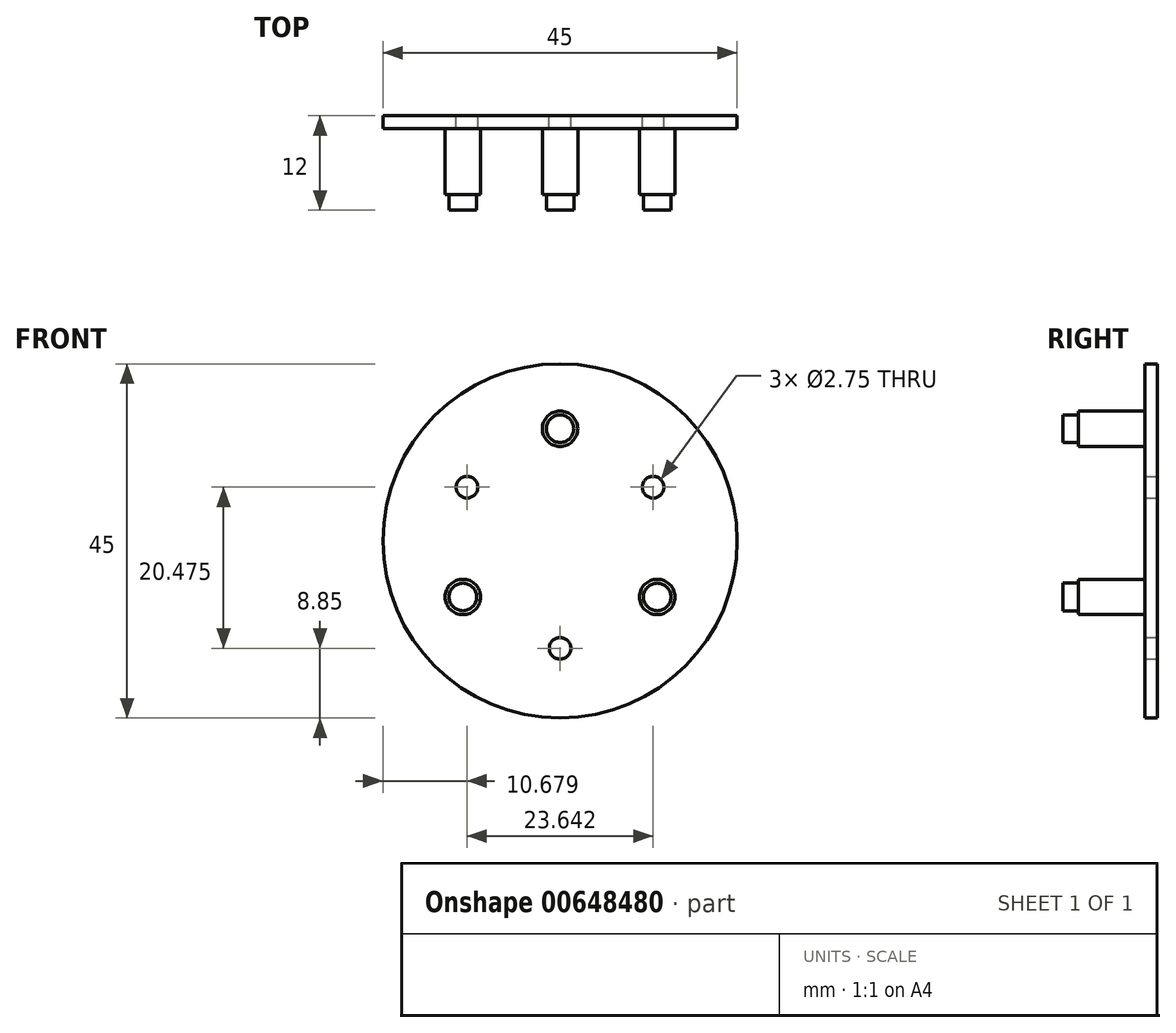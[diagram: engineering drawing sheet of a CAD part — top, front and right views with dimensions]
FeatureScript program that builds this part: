
annotation { "Feature Type Name" : "Feature", "Feature Type Description" : "" }
export const myFeature = defineFeature(function(context is Context, id is Id, definition is map)
    precondition{}
    {
        {
            var Q0;
            Q0=qCreatedBy(makeId("Front.planeOp"),FACE);
            var sketch = newSketch(context, id + "F0", { "sketchPlane" : qUnion([Q0])});
            skCircle(sketch, "E0", {"center": v(0, 0) * mm, "radius": 22.5 * mm});
            skSolve(sketch);
        }
        {
            var Q0;
            Q0=makeQuery(id+"F0.imprint","IMPRINT",FACE,{"disambiguationData":[TD([[makeQuery(id+"F0.imprint","IMPRINT",EDGE,{"derivedFrom":sQuery(id+"F0.wireOp",EDGE,"E0")}),1.0]])]});
            extrude(context, id + "F1", {"entities" : qUnion([Q0]), "depth" : 1.6 * mm, "offsetDistance" : 25 * mm});
        }
        {
            var Q0;
            Q0=makeQuery(id+"F1.opExtrude","CAP_FACE",FACE,{"disambiguationData":[OSD([sQuery(id+"F0.wireOp",EDGE,"E0")])],"isStart":true});
            var sketch = newSketch(context, id + "F2", { "sketchPlane" : qUnion([Q0])});
            skPoint(sketch, "E1", {"position": v(0, 14.25) * mm});
            skPoint(sketch, "E2.1.0", {"position": v(-12.34, -7.12) * mm});
            skPoint(sketch, "E2.2.0", {"position": v(12.34, -7.13) * mm});
            skPoint(sketch, "E2.center", {"position": v(0, 0) * mm});
            skCircle(sketch, "E3", {"center": v(0, 14.25) * mm, "radius": 2.25 * mm});
            skCircle(sketch, "E4", {"center": v(-12.34, -7.12) * mm, "radius": 2.25 * mm});
            skCircle(sketch, "E5", {"center": v(12.34, -7.13) * mm, "radius": 2.25 * mm});
            skSolve(sketch);
        }
        {
            var Q0;
            Q0=makeQuery(id+"F1.opExtrude","CAP_FACE",FACE,{"disambiguationData":[OSD([sQuery(id+"F0.wireOp",EDGE,"E0")])],"isStart":true});
            var sketch = newSketch(context, id + "F3", { "sketchPlane" : qUnion([Q0])});
            skPoint(sketch, "E6", {"position": v(0, -13.65) * mm});
            skPoint(sketch, "E7.1.0", {"position": v(11.82, 6.82) * mm});
            skPoint(sketch, "E7.2.0", {"position": v(-11.82, 6.83) * mm});
            skPoint(sketch, "E7.center", {"position": v(0, 0) * mm});
            skSolve(sketch);
        }
        {
            var Q0;
            Q0=sQuery(id+"F3.wireOp",VERTEX,"E7.1.0");
            var Q1;
            Q1=sQuery(id+"F3.wireOp",VERTEX,"E6");
            var Q2;
            Q2=sQuery(id+"F3.wireOp",VERTEX,"E7.2.0");
            var Q3;
            Q3=makeQuery(id+"F1.opExtrude","SWEPT_BODY",BODY,{"disambiguationData":[OSD([sQuery(id+"F0.wireOp",EDGE,"E0")])]});
            hole(context, id + "F4", {"style" : HoleStyle.SIMPLE, "endStyle" : HoleEndStyle.THROUGH, "holeDiameter" : 2.75 * mm, "majorDiameter" : 5 * mm, "isTappedThrough" : true, "tappedDepth" : 12 * mm, "tapClearance" : 3, "locations" : qUnion([Q0, Q1, Q2]), "scope" : qUnion([Q3])});
        }
        {
            var Q0;
            Q0 = qSketchRegion(id + "F2", true);
            extrude(context, id + "F5", {"entities" : qUnion([Q0]), "operationType" : NewBodyOperationType.ADD, "oppositeDirection" : true, "depth" : 10 * mm, "offsetDistance" : 25 * mm});
        }
        {
            var Q0;
            Q0=makeQuery(id+"F5.opExtrude","CAP_FACE",FACE,{"disambiguationData":[OSD([sQuery(id+"F2.wireOp",EDGE,"E3")])],"isStart":false});
            var sketch = newSketch(context, id + "F6", { "sketchPlane" : qUnion([Q0])});
            skCircle(sketch, "E8", {"center": v(0, 14.25) * mm, "radius": 1.75 * mm});
            skSolve(sketch);
        }
        {
            var Q0;
            Q0=makeQuery(id+"F5.opExtrude","CAP_FACE",FACE,{"disambiguationData":[OSD([sQuery(id+"F2.wireOp",EDGE,"E5")])],"isStart":false});
            var sketch = newSketch(context, id + "F7", { "sketchPlane" : qUnion([Q0])});
            skCircle(sketch, "E9", {"center": v(-12.34, -7.13) * mm, "radius": 1.75 * mm});
            skSolve(sketch);
        }
        {
            var Q0;
            Q0=makeQuery(id+"F5.opExtrude","CAP_FACE",FACE,{"disambiguationData":[OSD([sQuery(id+"F2.wireOp",EDGE,"E4")])],"isStart":false});
            var sketch = newSketch(context, id + "F8", { "sketchPlane" : qUnion([Q0])});
            skCircle(sketch, "E10", {"center": v(12.34, -7.12) * mm, "radius": 1.75 * mm});
            skSolve(sketch);
        }
        {
            var Q0;
            Q0=makeQuery(id+"F6.imprint","IMPRINT",FACE,{"disambiguationData":[TD([[makeQuery(id+"F6.imprint","IMPRINT",EDGE,{"derivedFrom":sQuery(id+"F6.wireOp",EDGE,"E8")}),1.0]])]});
            var Q1;
            Q1=makeQuery(id+"F7.imprint","IMPRINT",FACE,{"disambiguationData":[TD([[makeQuery(id+"F7.imprint","IMPRINT",EDGE,{"derivedFrom":sQuery(id+"F7.wireOp",EDGE,"E9")}),1.0]])]});
            var Q2;
            Q2=makeQuery(id+"F8.imprint","IMPRINT",FACE,{"disambiguationData":[TD([[makeQuery(id+"F8.imprint","IMPRINT",EDGE,{"derivedFrom":sQuery(id+"F8.wireOp",EDGE,"E10")}),1.0]])]});
            extrude(context, id + "F9", {"entities" : qUnion([Q0, Q1, Q2]), "operationType" : NewBodyOperationType.ADD, "depth" : 2 * mm, "offsetDistance" : 25 * mm});
        }
    });
